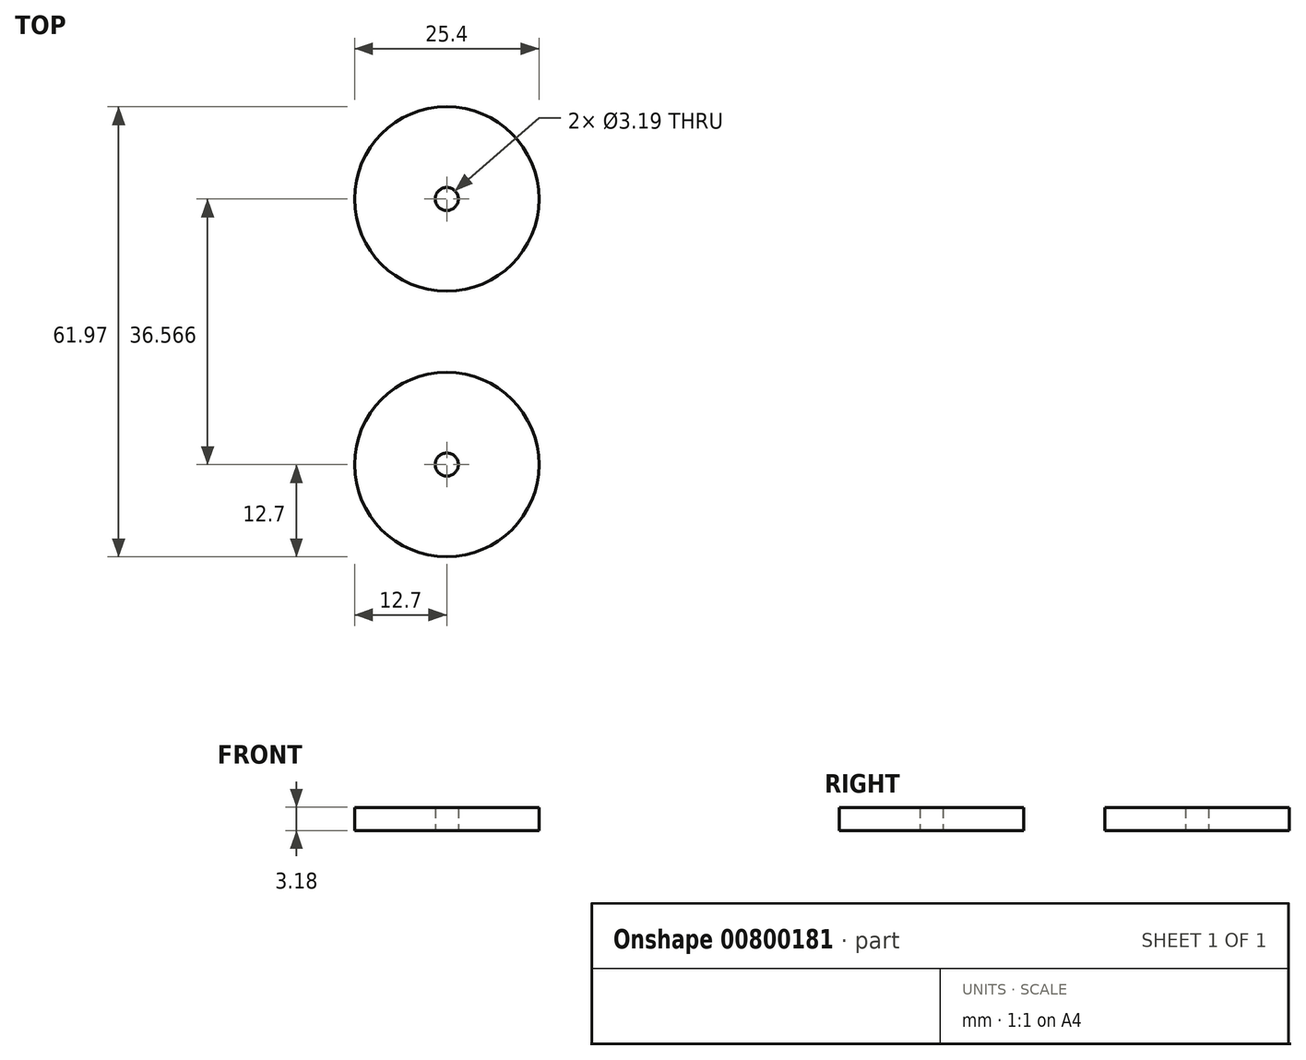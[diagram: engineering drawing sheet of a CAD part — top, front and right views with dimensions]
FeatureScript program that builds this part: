
annotation { "Feature Type Name" : "Feature", "Feature Type Description" : "" }
export const myFeature = defineFeature(function(context is Context, id is Id, definition is map)
    precondition{}
    {
        {
            var Q0;
            Q0=qCreatedBy(makeId("Top.planeOp"),FACE);
            var sketch = newSketch(context, id + "F0", { "sketchPlane" : qUnion([Q0])});
            skCircle(sketch, "E0", {"center": v(0, 0) * mm, "radius": 12.7 * mm});
            skCircle(sketch, "E1", {"center": v(0, 0) * mm, "radius": 1.6 * mm});
            skCircle(sketch, "E2", {"center": v(0, 36.57) * mm, "radius": 12.7 * mm});
            skCircle(sketch, "E3", {"center": v(0, 36.57) * mm, "radius": 1.6 * mm});
            skSolve(sketch);
        }
        {
            var Q0;
            Q0=makeQuery(id+"F0.imprint","IMPRINT",FACE,{"disambiguationData":[TD([[makeQuery(id+"F0.imprint","IMPRINT",EDGE,{"derivedFrom":sQuery(id+"F0.wireOp",EDGE,"E2")}),1.0]])]});
            var Q1;
            Q1=makeQuery(id+"F0.imprint","IMPRINT",FACE,{"disambiguationData":[TD([[makeQuery(id+"F0.imprint","IMPRINT",EDGE,{"derivedFrom":sQuery(id+"F0.wireOp",EDGE,"E0")}),1.0]])]});
            extrude(context, id + "F1", {"entities" : qUnion([Q0, Q1]), "depth" : 3.17 * mm, "offsetDistance" : 25.4 * mm});
        }
    });
